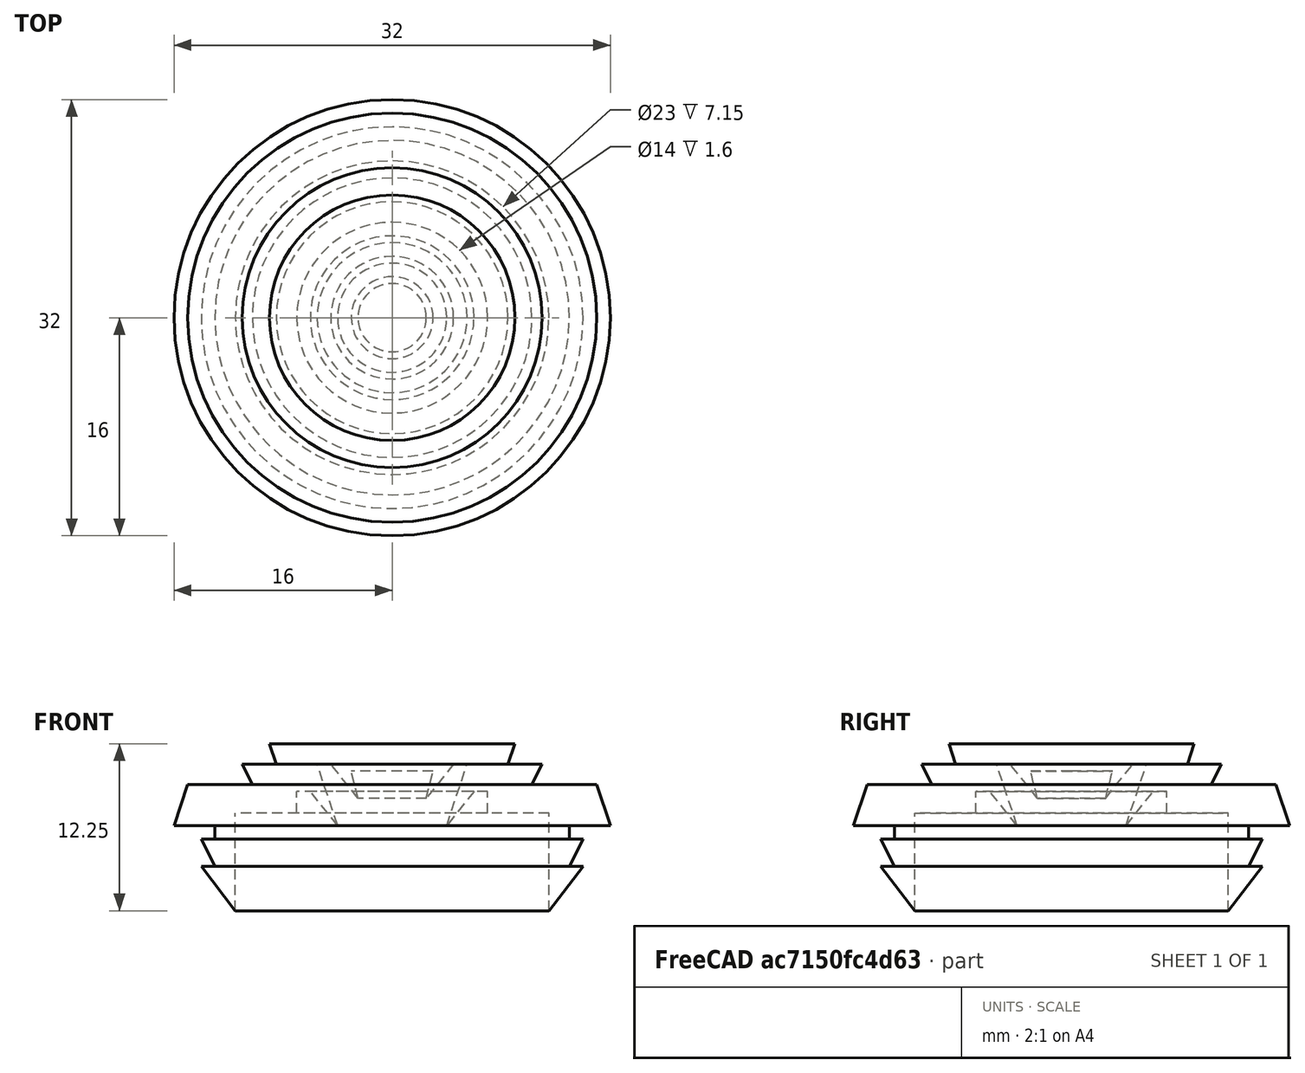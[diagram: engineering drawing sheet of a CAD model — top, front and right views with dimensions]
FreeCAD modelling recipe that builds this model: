
FCSTD DOCUMENT  (FreeCAD 0.15R4671 (Git))
Label: Tapón
License: CreativeCommons Attribution-ShareAlike
LicenseURL: http://creativecommons.org/licenses/by-sa/4.0/
objects: Sketcher::SketchObject×1, PartDesign::Revolution×1
note: 3 computed .brp shape members not serialized (recipe doc carries the construction recipe); baked Part::Feature solids carry a one-line shape summary decoded from their .brp

FEATURE [Sketcher::SketchObject] Sketch
  Placement = pos=(0,0,0) rot=(1,0,0;1.5708rad)
  sketch-geometry (23):
    g0: LineSegment StartX=0 StartY=10.25 StartZ=0 EndX=0 EndY=12.25 EndZ=0
    g1: LineSegment StartX=0 StartY=12.25 StartZ=0 EndX=9 EndY=12.25 EndZ=0
    g2: LineSegment StartX=9 StartY=12.25 StartZ=0 EndX=8.5 EndY=10.75 EndZ=0
    g3: LineSegment StartX=8.5 StartY=10.75 StartZ=0 EndX=11 EndY=10.75 EndZ=0
    g4: LineSegment StartX=11 StartY=10.75 StartZ=0 EndX=10.25 EndY=9.25 EndZ=0
    g5: LineSegment StartX=10.25 StartY=9.25 StartZ=0 EndX=15 EndY=9.25 EndZ=0
    g6: LineSegment StartX=15 StartY=9.25 StartZ=0 EndX=16 EndY=6.25 EndZ=0
    g7: LineSegment StartX=16 StartY=6.25 StartZ=0 EndX=13 EndY=6.25 EndZ=0
    g8: LineSegment StartX=13 StartY=6.25 StartZ=0 EndX=13 EndY=5.25 EndZ=0
    g9: LineSegment StartX=13 StartY=5.25 StartZ=0 EndX=14 EndY=5.25 EndZ=0
    g10: LineSegment StartX=14 StartY=5.25 StartZ=0 EndX=13 EndY=3.25 EndZ=0
    g11: LineSegment StartX=13 StartY=3.25 StartZ=0 EndX=14 EndY=3.25 EndZ=0
    g12: LineSegment StartX=14 StartY=3.25 StartZ=0 EndX=11.5 EndY=0 EndZ=0
    g13: LineSegment StartX=11.5 StartY=0 StartZ=0 EndX=11.5 EndY=7.15 EndZ=0
    g14: LineSegment StartX=11.5 StartY=7.15 StartZ=0 EndX=7 EndY=7.15 EndZ=0
    g15: LineSegment StartX=7 StartY=7.15 StartZ=0 EndX=7 EndY=8.75 EndZ=0
    g16: LineSegment StartX=7 StartY=8.75 StartZ=0 EndX=6 EndY=8.75 EndZ=0
    g17: LineSegment StartX=6 StartY=8.75 StartZ=0 EndX=4 EndY=6.25 EndZ=0
    g18: LineSegment StartX=4 StartY=6.25 StartZ=0 EndX=5.5 EndY=10.75 EndZ=0
    g19: LineSegment StartX=5.5 StartY=10.75 StartZ=0 EndX=4.5 EndY=10.75 EndZ=0
    g20: LineSegment StartX=4.5 StartY=10.75 StartZ=0 EndX=2.5 EndY=8.25 EndZ=0
    g21: LineSegment StartX=2.5 StartY=8.25 StartZ=0 EndX=3 EndY=10.25 EndZ=0
    g22: LineSegment StartX=3 StartY=10.25 StartZ=0 EndX=0 EndY=10.25 EndZ=0
  constraints (69):
    c: PointOnObject(g0,g-2)
    c: Coincident(g0,g1)
    c: Horizontal(g1)
    c: Coincident(g1,g2)
    c: Coincident(g2,g3)
    c: Horizontal(g3)
    c: Coincident(g3,g4)
    c: Coincident(g4,g5)
    c: Horizontal(g5)
    c: Coincident(g5,g6)
    c: Coincident(g6,g7)
    c: Horizontal(g7)
    c: Coincident(g7,g8)
    c: Vertical(g8)
    c: Coincident(g8,g9)
    c: Coincident(g9,g10)
    c: Coincident(g10,g11)
    c: Horizontal(g11)
    c: Coincident(g11,g12)
    c: PointOnObject(g12,g-1)
    c: Coincident(g12,g13)
    c: Coincident(g13,g14)
    c: Horizontal(g14)
    c: Coincident(g14,g15)
    c: Vertical(g15)
    c: Coincident(g15,g16)
    c: Coincident(g16,g17)
    c: Coincident(g17,g18)
    c: Coincident(g18,g19)
    c: Horizontal(g19)
    c: Coincident(g19,g20)
    c: Coincident(g20,g21)
    c: Coincident(g21,g22)
    c: Coincident(g22,g0)
    c: Horizontal(g22)
    c: PointOnObject(g0,g-2)
    c: DistanceX(g1,g1) = 9
    c: DistanceX(g-1,g2) = 8.5
    c: DistanceX(g-1,g3) = 11
    c: DistanceX(g-1,g4) = 10.25
    c: DistanceY(g2,g2) = 1.5
    c: DistanceY(g4,g4) = 1.5
    c: Horizontal(g16)
    c: Horizontal(g9)
    c: Vertical(g13)
    c: DistanceX(g-1,g5) = 15
    c: DistanceX(g-1,g6) = 16
    c: DistanceY(g6,g6) = 3
    c: DistanceX(g-1,g21) = 3
    c: DistanceX(g-1,g20) = 2.5
    c: DistanceY(g21,g21) = 2
    c: DistanceX(g-1,g19) = 4.5
    c: DistanceX(g19,g19) = 1
    c: DistanceX(g-1,g17) = 4
    c: DistanceY(g0,g0) = 2
    c: DistanceY(g18,g0) = 1.5
    c: DistanceY(g17,g0) = 6
    c: DistanceX(g16,g16) = 1
    c: DistanceY(g15,g0) = 3.5
    c: DistanceX(g0,g7) = 13
    c: DistanceY(g8,g8) = 1
    c: DistanceX(g0,g9) = 14
    c: DistanceY(g10,g10) = 2
    c: DistanceX(g0,g11) = 14
    c: DistanceX(g0,g16) = 6
    c: DistanceX(g-1,g12) = 11.5
    c: DistanceY(g12,g1) = 12.25
    c: DistanceY(g13,g13) = 7.15
    c: DistanceX(g0,g10) = 13
FEATURE [PartDesign::Revolution] Revolution
  Angle = 360
  Axis = (0,0,1)
  Base = (0,0,0)
  Placement = pos=(0,0,0) rot=(1,0,0;1.5708rad)
  ReferenceAxis = -> Sketch [V_Axis]
  Reversed = true
  Sketch = -> Sketch
